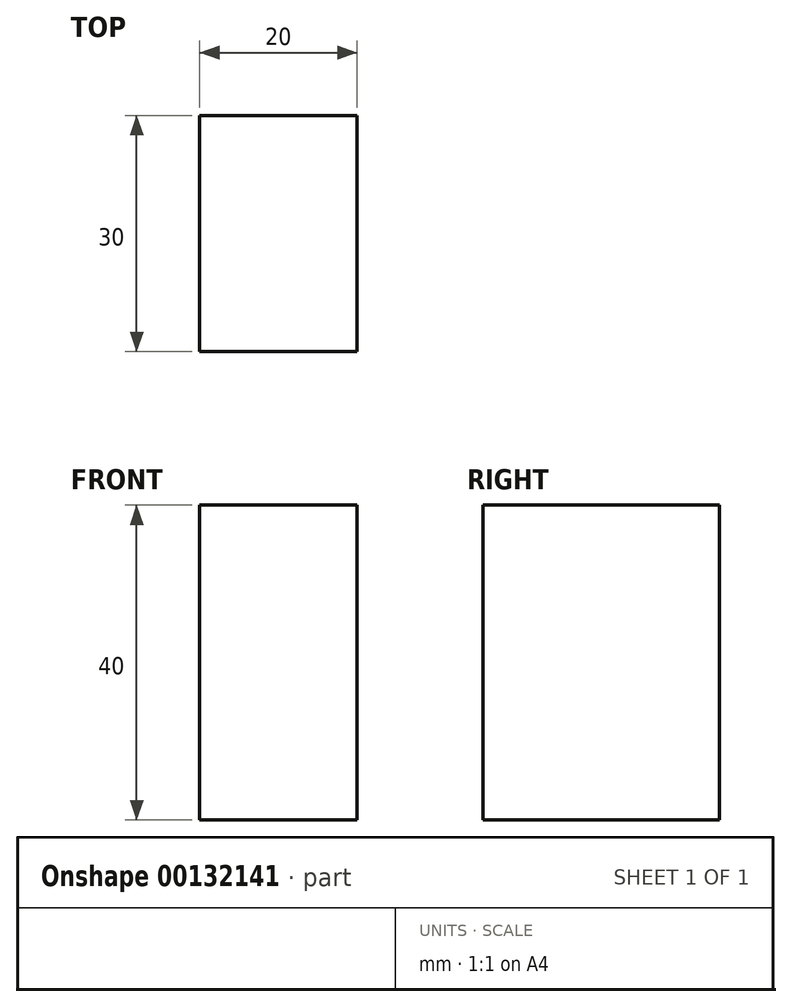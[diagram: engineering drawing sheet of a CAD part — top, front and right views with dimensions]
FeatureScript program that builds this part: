
annotation { "Feature Type Name" : "Feature", "Feature Type Description" : "" }
export const myFeature = defineFeature(function(context is Context, id is Id, definition is map)
    precondition{}
    {
        {
            var Q0;
            Q0=qCreatedBy(makeId("Top.planeOp"),FACE);
            var sketch = newSketch(context, id + "F0", { "sketchPlane" : qUnion([Q0])});
            skLineSegment(sketch, "E0.bottom", {"start": v(0, 0) * mm, "end": v(7000, 0) * mm});
            skSolve(sketch);
        }
        {
            var Q0;
            Q0 = qSketchRegion(id + "F0", true);
            var Q1;
            Q1=sQuery(id+"F0.wireOp",EDGE,"E0.left");
            var Q2;
            Q2=sQuery(id+"F0.wireOp",EDGE,"E0.top");
            var Q3;
            Q3=sQuery(id+"F0.wireOp",EDGE,"E0.right");
            var Q4;
            Q4=sQuery(id+"F0.wireOp",EDGE,"E0.bottom");
            extrude(context, id + "F1", {"entities" : qUnion([Q0]), "bodyType" : ToolBodyType.SURFACE, "surfaceEntities" : qUnion([Q1, Q2, Q3, Q4]), "depth" : 1 * mm});
        }
        {
            var Q0;
            Q0=qCreatedBy(makeId("Top.planeOp"),FACE);
            var sketch = newSketch(context, id + "F2", { "sketchPlane" : qUnion([Q0])});
            skLineSegment(sketch, "E1.bottom", {"start": v(0, 0) * mm, "end": v(20, 0) * mm});
            skLineSegment(sketch, "E1.top", {"start": v(0, 30) * mm, "end": v(20, 30) * mm});
            skLineSegment(sketch, "E1.left", {"start": v(0, 0) * mm, "end": v(0, 30) * mm});
            skLineSegment(sketch, "E1.right", {"start": v(20, 0) * mm, "end": v(20, 30) * mm});
            skSolve(sketch);
        }
        {
            var Q0;
            Q0=makeQuery(id+"F2.imprint","IMPRINT",FACE,{"disambiguationData":[TD([[makeQuery(id+"F2.imprint","IMPRINT",EDGE,{"derivedFrom":sQuery(id+"F2.wireOp",EDGE,"E1.bottom")}),1.0]])]});
            extrude(context, id + "F3", {"entities" : qUnion([Q0]), "depth" : 40 * mm});
        }
    });
